# Revit family: Grinder_Pumps-Progressing_Cavity-Zoeller-Sewage_Waste-810_815_Series
name_source: partatom
category: Mechanical Equipment
revit_build: Autodesk Revit 2014 (Build: 20130308_1515(x64)
units: mm (PartAtom-declared; Revit-internal decimal feet)

## types (2) — shared parameters
Cooling = Oil filled
Cord Length = 240"
Cord Type = SOW or SOOW, multi-wire neoprene
Default Elevation = 0"
Description = The Shark The Shark®. 810, 815 Series. Progressing cavity grinder pump.
Discharge Radius = 5/8"
Discharge Size = 1 1/4" NPT Horizontal
Height = 22 3/8"
Hertz = 60
Installation Type = Floor Mounted
Insulation = Class B
Length = 8"
Manufacturer = Zoeller
Material = Cast Iron-Zoeller-Powder Coated Epoxy
Max Flow Rate = 14.6 GPM (55.3 LPM)
Max. Operating Temp. = 54°C (130°F)
Mechanical Seals = Carbon/ceramic
Motor Protection = Auto reset thermal overload
Operation = Non-Automatic
Phase = 1 Ph
Price = Prices may vary. Please consult Manufacturer Representative for most up-to-date price list.
Product Page URL = http://www.zoellerpumps.com
RPM = 1725
Type = Permanent Split Capacitor
URL = http://www.zoellerpumps.com
Voltage = 230 V
Warranty Information = 36 Months (Limited)
Waste Connection = Yes
Width = 8 3/8"

## per-type parameters (varying)
| type | Amps | Apparent Load | Maximum Head | Model | Motor |
| E810 - 230V 1Ph | 7 A | 1610 VA | 150' (45.7 m) | 810 | 1 HP |
| E815 - 230V 1Ph | 11 A | 2415 VA | 240' (73.1 m) | 815 | 2 HP |

## geometry (parser evidence)
native form markers: Sweep x1
no freeform markers — native parametric forms only
